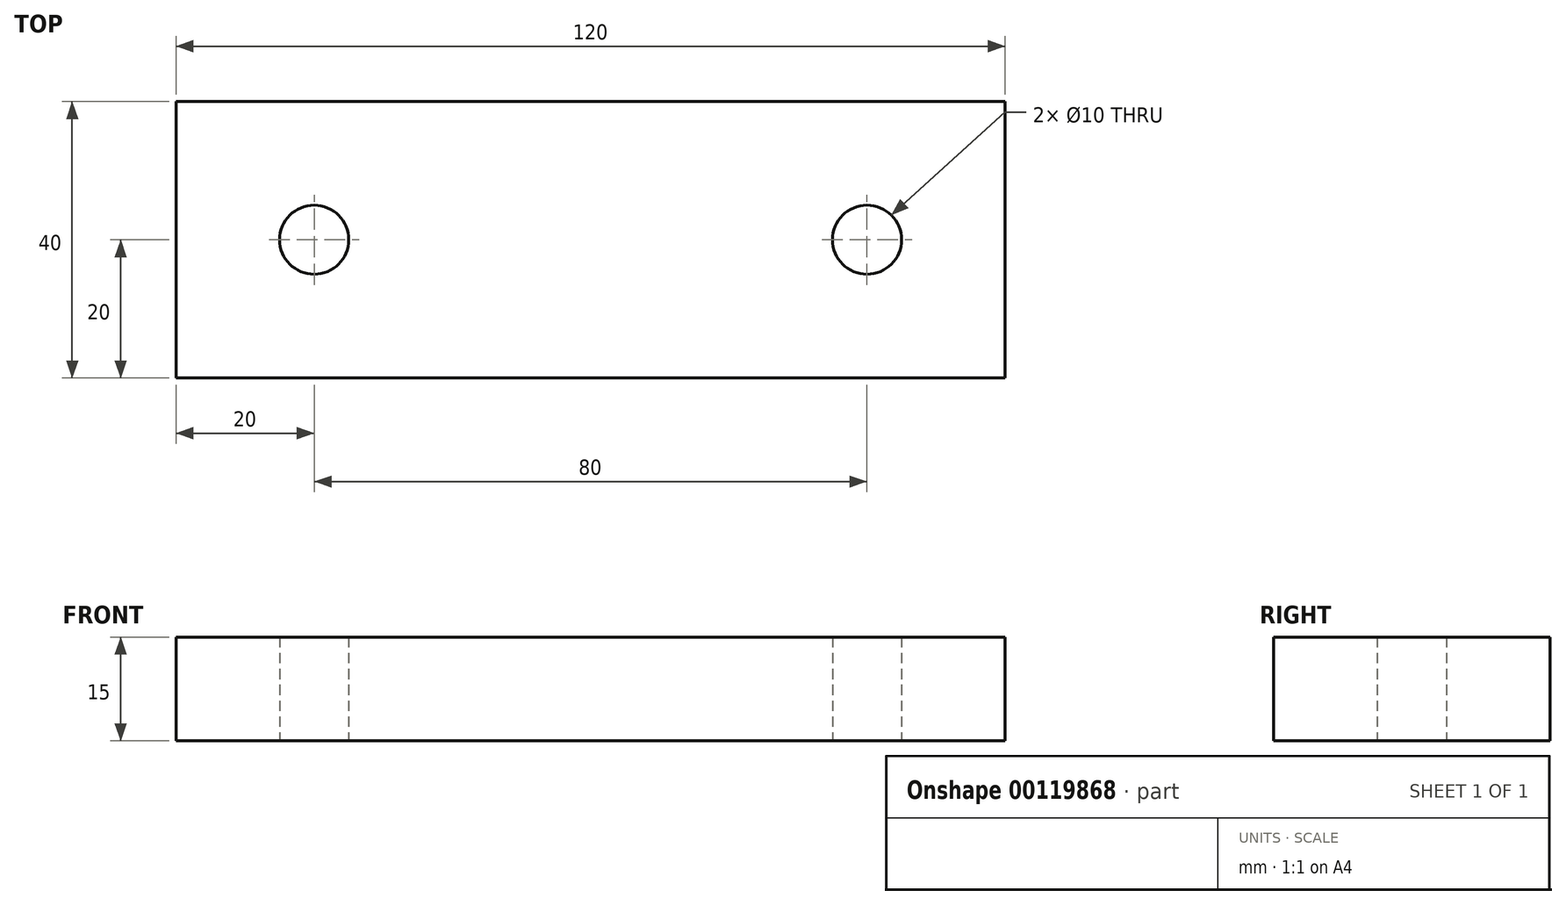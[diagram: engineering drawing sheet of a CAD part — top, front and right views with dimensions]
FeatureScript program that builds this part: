
annotation { "Feature Type Name" : "Feature", "Feature Type Description" : "" }
export const myFeature = defineFeature(function(context is Context, id is Id, definition is map)
    precondition{}
    {
        {
            var Q0;
            Q0=qCreatedBy(makeId("Top.planeOp"),FACE);
            var sketch = newSketch(context, id + "F0", { "sketchPlane" : qUnion([Q0])});
            skLineSegment(sketch, "E0.bottom", {"start": v(0, 0) * mm, "end": v(120, 0) * mm});
            skLineSegment(sketch, "E0.top", {"start": v(0, 40) * mm, "end": v(120, 40) * mm});
            skLineSegment(sketch, "E0.left", {"start": v(0, 0) * mm, "end": v(0, 40) * mm});
            skLineSegment(sketch, "E0.right", {"start": v(120, 0) * mm, "end": v(120, 40) * mm});
            skLineSegment(sketch, "E1", {"start": v(0, 0) * mm, "end": v(0, 20) * mm, "construction": true});
            skLineSegment(sketch, "E2", {"start": v(0, 20) * mm, "end": v(20, 20) * mm, "construction": true});
            skLineSegment(sketch, "E3", {"start": v(20, 20) * mm, "end": v(100, 20) * mm, "construction": true});
            skCircle(sketch, "E4", {"center": v(20, 20) * mm, "radius": 5 * mm});
            skCircle(sketch, "E5", {"center": v(100, 20) * mm, "radius": 5 * mm});
            skSolve(sketch);
        }
        {
            var Q0;
            Q0=makeQuery(id+"F0.imprint","IMPRINT",FACE,{"disambiguationData":[TD([[makeQuery(id+"F0.imprint","IMPRINT",EDGE,{"derivedFrom":sQuery(id+"F0.wireOp",EDGE,"E0.bottom")}),1.0]])]});
            extrude(context, id + "F1", {"entities" : qUnion([Q0]), "depth" : 15 * mm});
        }
    });
